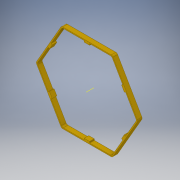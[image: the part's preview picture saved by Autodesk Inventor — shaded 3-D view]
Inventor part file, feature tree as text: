
AUTODESK INVENTOR PART (.ipt)
format: ipt  version: 2019 (Build 230136000, 136)  size: 499,712 bytes
history: native  units: mm
features: projected_geometry x14, extrude x9, sketch x9, pattern_circular x3, fillet x2, other x1
ambient origin geometry x8: Origin, YZ Plane, XZ Plane, XY Plane, X Axis, Y Axis, Z Axis, Center Point
bodies: Solid1 (feature_tree)
feature tree (38):
  extrude  "Extrusion1"  Depth=2.0mm
  extrude  "Extrusion5"  Depth=2.0mm
  extrude  "Extrusion6"  Depth=10.0mm
  fillet  "Fillet1"  [1 undecoded]
  fillet  "Fillet2"  Radius=4.0mm
  extrude  "Extrusion7"  TaperAngle=0.0deg  [1 undecoded]
  extrude  "Extrusion8"  Depth=4.0mm
  other  "Work Axis2"
  pattern_circular  "Circular Pattern1"  [2 undecoded]
  extrude  "Extrusion9"  Depth=3.0mm
  extrude  "Extrusion10"  Depth=10.0mm
  extrude  "Extrusion11"  TaperAngle=0.0deg  [1 undecoded]
  pattern_circular  "Circular Pattern2"  Count=6  [1 undecoded]
  extrude  "Extrusion12"  TaperAngle=360.0deg  [1 undecoded]
  pattern_circular  "Circular Pattern3"  [2 undecoded]
  sketch  "Sketch1"  dims[d0=175.0mm d1=2.0mm]
  sketch  "Sketch5"  dims[d2=0.0mm d15=2.0mm]
  projected_geometry  "Projected Loop4"
  sketch  "Sketch7"  dims[d16=2.0mm d17=10.0mm d18=0.0mm d19=4.0mm]
  projected_geometry  "Projected Loop6"
  sketch  "Sketch8"  dims[d20=7.0mm d21=0.0mm]
  sketch  "Sketch9"  dims[d22=10.0mm d23=4.0mm]
  projected_geometry  "Projected Loop7"
  sketch  "Sketch11"  dims[d24=10.0mm]
  projected_geometry  "Projected Loop8"
  sketch  "Sketch12"  dims[d25=3.3mm]
  projected_geometry  "Projected Loop9"
  projected_geometry  "Projected Loop10"
  projected_geometry  "Projected Loop11"
  projected_geometry  "Projected Loop12"
  projected_geometry  "Projected Loop13"
  projected_geometry  "Projected Loop14"
  sketch  "Sketch13"  dims[d26=6.5mm]
  projected_geometry  "Projected Loop15"
  projected_geometry  "Projected Loop16"
  projected_geometry  "Projected Loop17"
  sketch  "Sketch14"  dims[d27=0.0mm d28=4.0mm d29=3.0mm d30=5.0mm d31=0.0mm d32=60.0mm d33=360.0deg d35=3.0mm d36=0.0mm d37=3.0mm d38=0.0mm d39=3.5mm d40=0.0mm d41=60.0mm d42=360.0deg d44=0.7mm d45=0.7mm d46=0.7mm d47=10.0mm d48=0.0mm d49=60.0mm d50=360.0deg]
  projected_geometry  "Projected Loop18"
note: 9 required parameter values undecoded (feature->parameter linkage not recoverable at this tier; creation-order binding heuristic only, values carry confidence <= 0.55)
